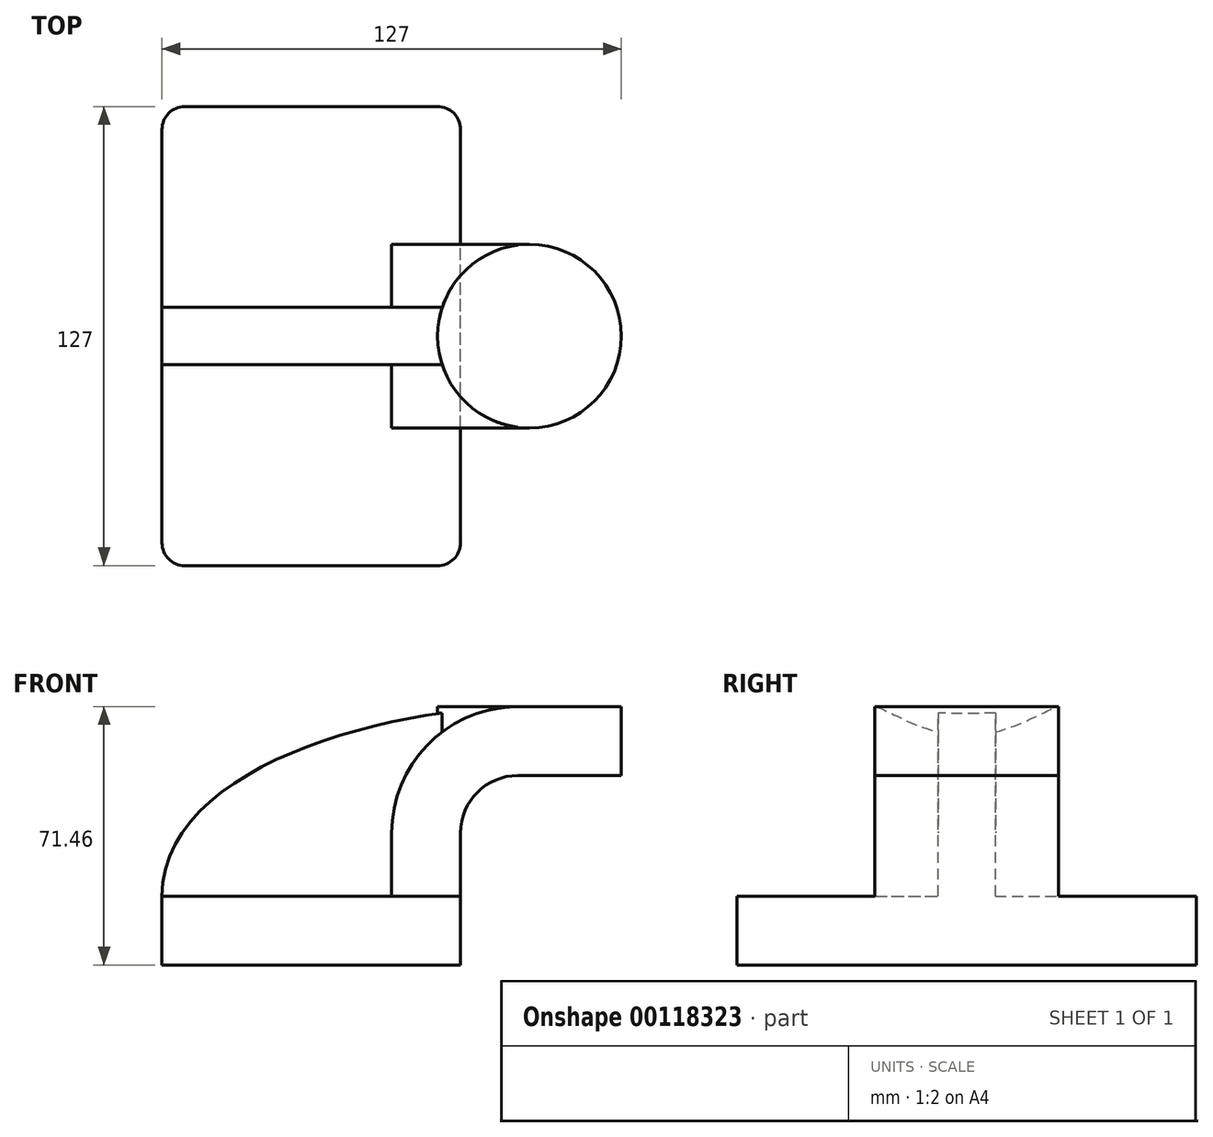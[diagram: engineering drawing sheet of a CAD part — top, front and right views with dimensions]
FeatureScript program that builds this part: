
annotation { "Feature Type Name" : "Feature", "Feature Type Description" : "" }
export const myFeature = defineFeature(function(context is Context, id is Id, definition is map)
    precondition{}
    {
        {
            var Q0;
            Q0=qCreatedBy(makeId("Front.planeOp"),FACE);
            var sketch = newSketch(context, id + "F0", { "sketchPlane" : qUnion([Q0])});
            skLineSegment(sketch, "E0.bottom", {"start": v(-41.28, -9.53) * mm, "end": v(41.28, -9.53) * mm});
            skLineSegment(sketch, "E0.top", {"start": v(-41.28, 9.52) * mm, "end": v(41.28, 9.52) * mm});
            skLineSegment(sketch, "E0.left", {"start": v(-41.28, -9.53) * mm, "end": v(-41.28, 9.52) * mm});
            skLineSegment(sketch, "E0.right", {"start": v(41.28, -9.53) * mm, "end": v(41.28, 9.52) * mm});
            skPoint(sketch, "E0.middle", {"position": v(0, 0) * mm});
            skLineSegment(sketch, "E1.bottom", {"start": v(60.33, 38.1) * mm, "end": v(111.13, 38.1) * mm});
            skLineSegment(sketch, "E1.top", {"start": v(60.33, 66.67) * mm, "end": v(111.13, 66.67) * mm});
            skLineSegment(sketch, "E1.left", {"start": v(60.33, 38.1) * mm, "end": v(60.33, 66.67) * mm});
            skLineSegment(sketch, "E1.right", {"start": v(111.13, 38.1) * mm, "end": v(111.13, 66.67) * mm});
            skPoint(sketch, "E1.middle", {"position": v(85.73, 52.39) * mm});
            skLineSegment(sketch, "E2", {"start": v(41.27, 9.52) * mm, "end": v(41.27, 27) * mm});
            skArc(sketch, "E3", {"start": v(41.27, 27) * mm, "mid": v(45.92, 38.23) * mm, "end": v(57.15, 42.88) * mm});
            skLineSegment(sketch, "E4", {"start": v(57.15, 42.88) * mm, "end": v(85.72, 42.88) * mm});
            skLineSegment(sketch, "E5.0", {"start": v(57.15, 61.93) * mm, "end": v(85.72, 61.93) * mm});
            skArc(sketch, "E5.1", {"start": v(22.22, 27) * mm, "mid": v(32.45, 51.7) * mm, "end": v(57.15, 61.93) * mm});
            skLineSegment(sketch, "E5.2", {"start": v(22.22, 9.52) * mm, "end": v(22.22, 27) * mm});
            skLineSegment(sketch, "E6", {"start": v(85.73, 38.1) * mm, "end": v(85.72, 61.93) * mm});
            skFitSpline(sketch, "E7", {"points": [v(-41.28, 9.52) * mm, v(57.15, 61.93) * mm], "startDerivative": vector(0.42, 108.24) * mm, "endDerivative": vector(109.21, 1.75) * mm});
            skSolve(sketch);
        }
        {
            var Q0;
            Q0=makeQuery(id+"F0.imprint","IMPRINT",FACE,{"disambiguationData":[TD([[makeQuery(id+"F0.imprint","IMPRINT",EDGE,{"derivedFrom":sQuery(id+"F0.wireOp",EDGE,"E0.bottom")}),1.0]])]});
            extrude(context, id + "F1", {"entities" : qUnion([Q0]), "endBound" : BoundingType.SYMMETRIC, "depth" : 127 * mm});
        }
        {
            var Q0;
            {var subQ6=sQuery(id+"F0.wireOp",EDGE,"E2");Q0=makeQuery(id+"F0.imprint","IMPRINT",FACE,{"disambiguationData":[TD([[makeQuery(id+"F0.imprint","IMPRINT",EDGE,{"derivedFrom":subQ6}),1.0]])]});}
            extrude(context, id + "F2", {"entities" : qUnion([Q0]), "operationType" : NewBodyOperationType.ADD, "endBound" : BoundingType.SYMMETRIC, "depth" : 50.8 * mm});
        }
        {
            var Q0;
            {var subQ3=sQuery(id+"F0.wireOp",EDGE,"E5.2");Q0=makeQuery(id+"F0.imprint","IMPRINT",FACE,{"disambiguationData":[TD([[makeQuery(id+"F0.imprint","IMPRINT",EDGE,{"derivedFrom":subQ3}),1.0]])]});}
            extrude(context, id + "F3", {"entities" : qUnion([Q0]), "operationType" : NewBodyOperationType.ADD, "endBound" : BoundingType.SYMMETRIC, "depth" : 15.88 * mm});
        }
        {
            var Q0;
            {var subQ0=sQuery(id+"F0.wireOp",EDGE,"E4");var subQ1=sQuery(id+"F0.wireOp",EDGE,"E1.left");var subQ2=makeQuery(id+"F0.imprint","INTERSECT",VERTEX,{"derivedFrom":[subQ1,subQ0]});Q0=makeQuery(id+"F0.imprint","IMPRINT",FACE,{"disambiguationData":[TD([[makeQuery(id+"F0.imprint","IMPRINT",EDGE,{"disambiguationData":[TD([[subQ2,-1.0]])],"derivedFrom":subQ1}),-1.0]])]});}
            var Q1;
            Q1=sQuery(id+"F0.wireOp",EDGE,"E1.left");
            revolve(context, id + "F4", {"operationType" : NewBodyOperationType.ADD, "entities" : qUnion([Q0]), "axis" : qUnion([Q1]), "revolveType" : RevolveType.FULL});
        }
        {
            var Q0;
            Q0=makeQuery(id+"F1.opExtrude","CAP_EDGE",EDGE,{"disambiguationData":[OSD([sQuery(id+"F0.wireOp",EDGE,"E0.left")])],"isStart":true});
            var Q1;
            Q1=makeQuery(id+"F1.opExtrude","CAP_EDGE",EDGE,{"disambiguationData":[OSD([sQuery(id+"F0.wireOp",EDGE,"E0.right")])],"isStart":true});
            var Q2;
            Q2=makeQuery(id+"F1.opExtrude","CAP_EDGE",EDGE,{"disambiguationData":[OSD([sQuery(id+"F0.wireOp",EDGE,"E0.left")])],"isStart":false});
            var Q3;
            Q3=makeQuery(id+"F1.opExtrude","CAP_EDGE",EDGE,{"disambiguationData":[OSD([sQuery(id+"F0.wireOp",EDGE,"E0.right")])],"isStart":false});
            fillet(context, id + "F5", {"entities" : qUnion([Q0, Q1, Q2, Q3]), "radius" : 6.35 * mm, "tangentPropagation" : true, "allowEdgeOverflow" : false});
        }
    });
